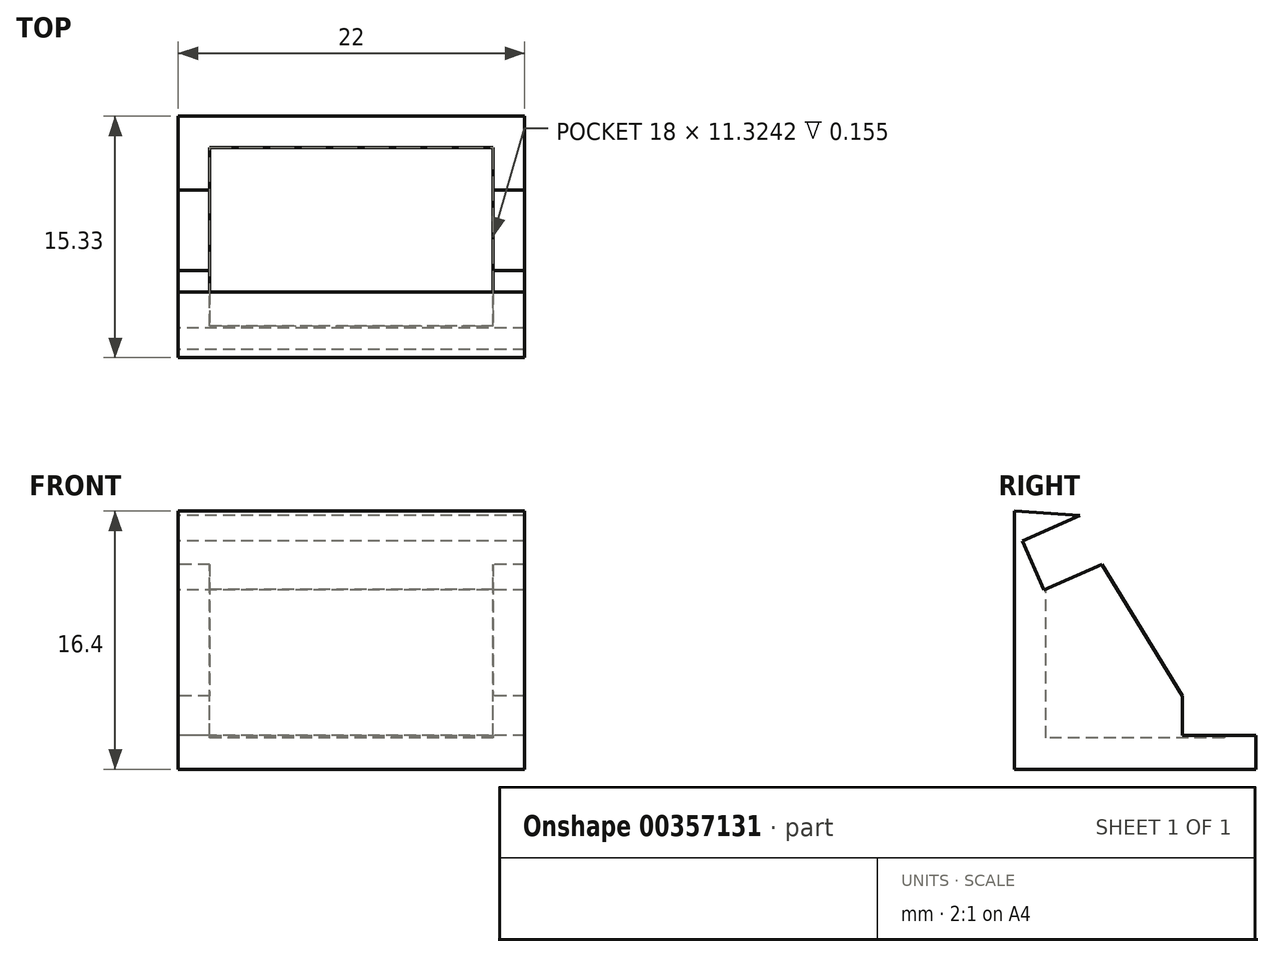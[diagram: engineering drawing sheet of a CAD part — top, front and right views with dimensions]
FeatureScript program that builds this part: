
annotation { "Feature Type Name" : "Feature", "Feature Type Description" : "" }
export const myFeature = defineFeature(function(context is Context, id is Id, definition is map)
    precondition{}
    {
        {
            var Q0;
            Q0=qCreatedBy(makeId("Right.planeOp"),FACE);
            var sketch = newSketch(context, id + "F0", { "sketchPlane" : qUnion([Q0])});
            skLineSegment(sketch, "E0", {"start": v(-24.83, 0) * mm, "end": v(-45.78, 0) * mm});
            skLineSegment(sketch, "E1", {"start": v(-45.78, 0) * mm, "end": v(-45.78, 16.4) * mm});
            skLineSegment(sketch, "E2", {"start": v(-41.62, 16.11) * mm, "end": v(-45.78, 16.4) * mm});
            skLineSegment(sketch, "E3", {"start": v(-41.62, 16.11) * mm, "end": v(-40.25, 13) * mm});
            skLineSegment(sketch, "E4", {"start": v(-40.25, 13) * mm, "end": v(-35.13, 4.65) * mm});
            skLineSegment(sketch, "E5", {"start": v(-35.13, 4.65) * mm, "end": v(-30.45, 4.66) * mm});
            skLineSegment(sketch, "E6", {"start": v(-30.45, 4.66) * mm, "end": v(-30.45, 0) * mm});
            skSolve(sketch);
        }
        {
            var Q0;
            Q0 = qSketchRegion(id + "F0", true);
            extrude(context, id + "F1", {"entities" : qUnion([Q0]), "depth" : 22 * mm});
        }
        {
            var Q0;
            Q0=makeQuery(id+"F1.opExtrude","SWEPT_FACE",FACE,{"disambiguationData":[OSD([sQuery(id+"F0.wireOp",EDGE,"z6AZPvvp-nOSF-rSed-l6pi-vFl7p4PYBzKS")])]});
            var Q1;
            Q1=makeQuery(id+"F1.opExtrude","SWEPT_FACE",FACE,{"disambiguationData":[OSD([sQuery(id+"F0.wireOp",EDGE,"53ceXSN1-mY1n-5oaW-UicX-xqiVoSkcZTxC")])]});
            var Q2;
            Q2=makeQuery(id+"F1.opExtrude","SWEPT_FACE",FACE,{"disambiguationData":[OSD([sQuery(id+"F0.wireOp",EDGE,"E4")])]});
            shell(context, id + "F2", {"entities" : qUnion([Q0, Q1, Q2]), "thickness" : 2 * mm});
        }
        {
            var Q0;
            Q0=makeQuery(id+"F1.opExtrude","SWEPT_FACE",FACE,{"disambiguationData":[OSD([sQuery(id+"F0.wireOp",EDGE,"stLy6wJ1-Ligu-mupm-dfyj-ddqptQbXcM57")])]});
            var Q1;
            Q1=makeQuery(id+"F1.opExtrude","SWEPT_FACE",FACE,{"disambiguationData":[OSD([sQuery(id+"F0.wireOp",EDGE,"E3")])]});
            extrude(context, id + "F3", {"entities" : qUnion([Q0, Q1]), "operationType" : NewBodyOperationType.REMOVE, "oppositeDirection" : true, "depth" : 4 * mm});
        }
        {
            var Q0;
            Q0=makeQuery(id+"F1.opExtrude","SWEPT_FACE",FACE,{"disambiguationData":[OSD([sQuery(id+"F0.wireOp",EDGE,"E5")])]});
            extrude(context, id + "F4", {"entities" : qUnion([Q0]), "operationType" : NewBodyOperationType.REMOVE, "oppositeDirection" : true, "depth" : 2.5 * mm});
        }
    });
